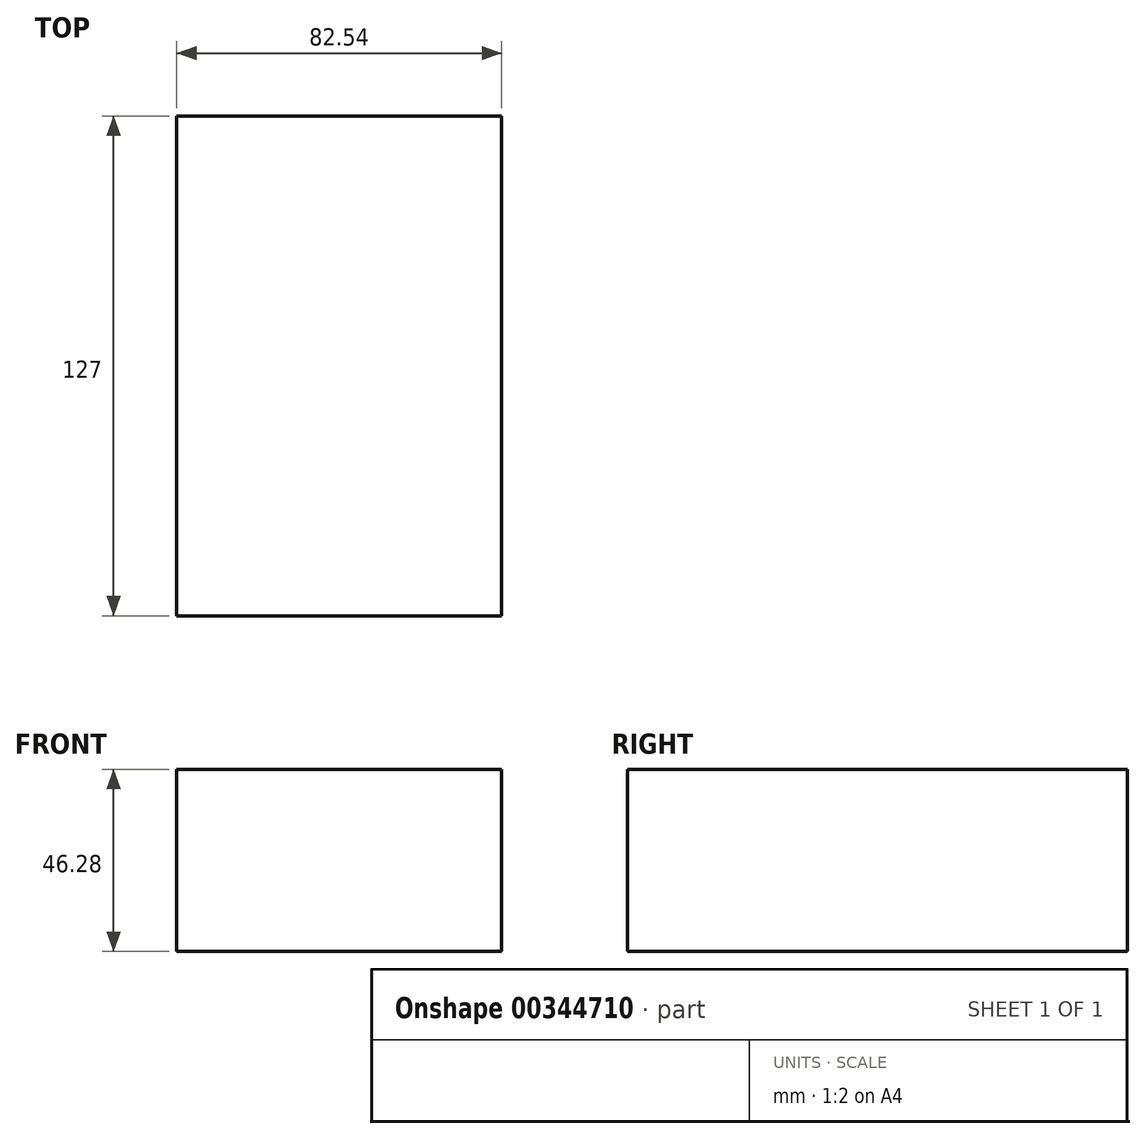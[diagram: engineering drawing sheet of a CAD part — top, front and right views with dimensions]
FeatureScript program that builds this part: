
annotation { "Feature Type Name" : "Feature", "Feature Type Description" : "" }
export const myFeature = defineFeature(function(context is Context, id is Id, definition is map)
    precondition{}
    {
        {
            var Q0;
            Q0=qCreatedBy(makeId("Front.planeOp"),FACE);
            var sketch = newSketch(context, id + "F0", { "sketchPlane" : qUnion([Q0])});
            skLineSegment(sketch, "E0.bottom", {"start": v(41.28, 23.14) * mm, "end": v(-41.28, 23.14) * mm});
            skLineSegment(sketch, "E0.top", {"start": v(41.28, -23.14) * mm, "end": v(-41.28, -23.14) * mm});
            skLineSegment(sketch, "E0.left", {"start": v(41.28, 23.14) * mm, "end": v(41.28, -23.14) * mm});
            skLineSegment(sketch, "E0.right", {"start": v(-41.28, 23.14) * mm, "end": v(-41.28, -23.14) * mm});
            skPoint(sketch, "E0.middle", {"position": v(0, 0) * mm});
            skPoint(sketch, "E1.middle", {"position": v(85.72, 38.77) * mm});
            skLineSegment(sketch, "E2", {"start": v(41.28, 23.14) * mm, "end": v(41.28, 23.62) * mm});
            skArc(sketch, "E3", {"start": v(41.28, 23.62) * mm, "mid": v(45.22, 33.13) * mm, "end": v(54.73, 37.07) * mm});
            skLineSegment(sketch, "E4", {"start": v(54.73, 37.07) * mm, "end": v(98.4, 37.07) * mm});
            skLineSegment(sketch, "E5.0", {"start": v(54.73, 56.12) * mm, "end": v(98.4, 56.12) * mm});
            skArc(sketch, "E5.1", {"start": v(22.23, 23.62) * mm, "mid": v(31.74, 46.6) * mm, "end": v(54.73, 56.12) * mm});
            skLineSegment(sketch, "E6", {"start": v(98.4, 56.12) * mm, "end": v(98.4, 37.07) * mm});
            skSolve(sketch);
        }
        {
            var Q0;
            Q0 = qSketchRegion(id + "F0", true);
            extrude(context, id + "F1", {"entities" : qUnion([Q0]), "oppositeDirection" : true, "depth" : 25.4 * mm});
        }
        {
            var Q0;
            Q0=makeQuery(id+"F0.imprint","IMPRINT",FACE,{"disambiguationData":[TD([[makeQuery(id+"F0.imprint","IMPRINT",EDGE,{"derivedFrom":sQuery(id+"F0.wireOp",EDGE,"E0.bottom")}),1.0]])]});
            extrude(context, id + "F2", {"entities" : qUnion([Q0]), "operationType" : NewBodyOperationType.ADD, "endBound" : BoundingType.SYMMETRIC, "depth" : 127 * mm});
        }
    });
